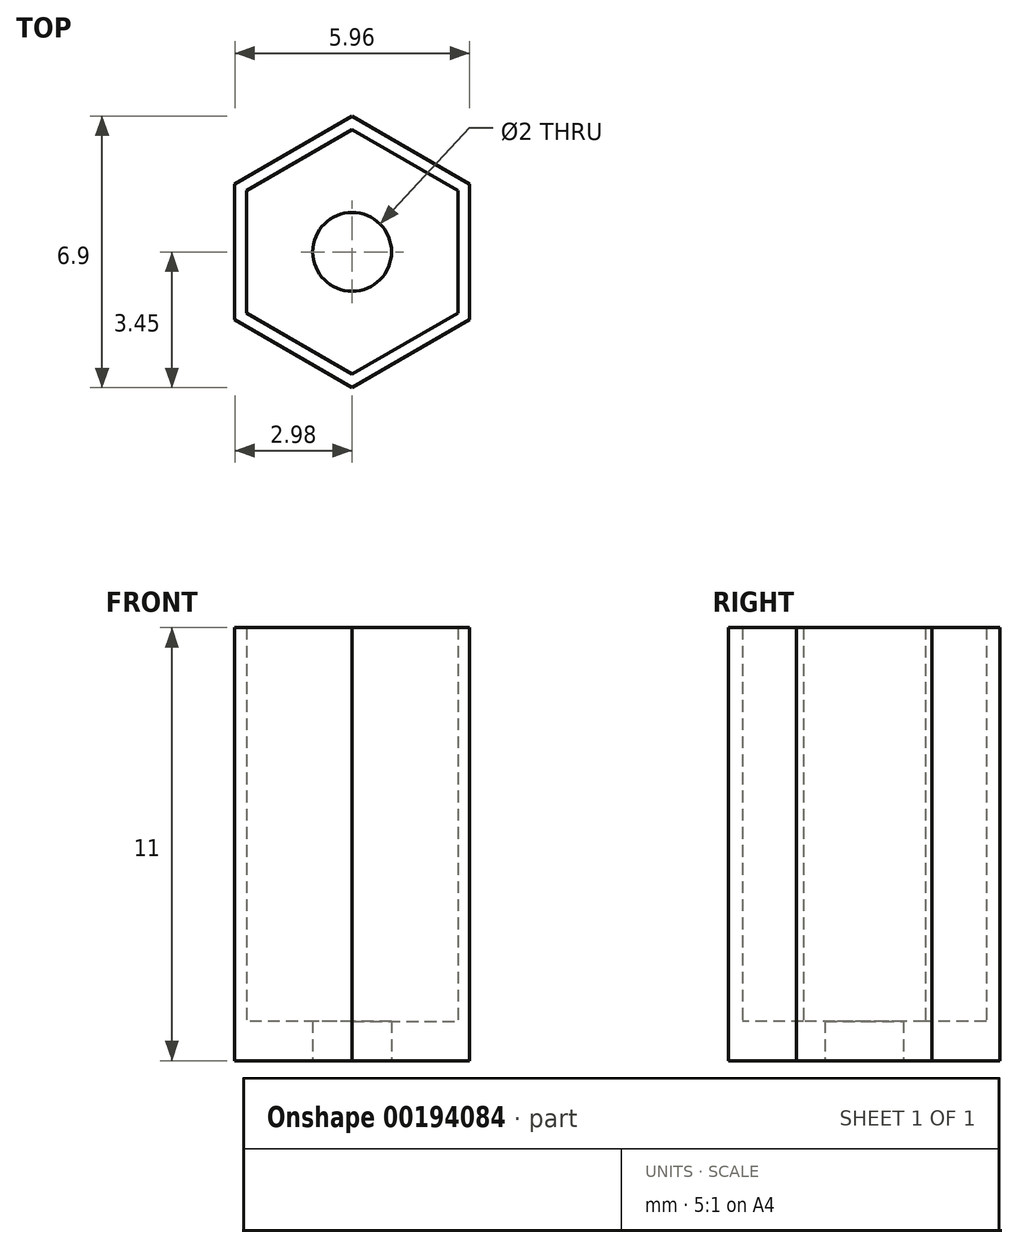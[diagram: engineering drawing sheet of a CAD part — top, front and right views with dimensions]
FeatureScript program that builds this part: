
annotation { "Feature Type Name" : "Feature", "Feature Type Description" : "" }
export const myFeature = defineFeature(function(context is Context, id is Id, definition is map)
    precondition{}
    {
        {
            var Q0;
            Q0=qCreatedBy(makeId("Top.planeOp"),FACE);
            var sketch = newSketch(context, id + "F0", { "sketchPlane" : qUnion([Q0])});
            skCircle(sketch, "E0.cCircle", {"center": v(0, 0) * mm, "radius": 2.68 * mm, "construction": true});
            skLineSegment(sketch, "E0.0", {"start": v(2.68, 1.55) * mm, "end": v(2.68, -1.55) * mm});
            skLineSegment(sketch, "E0.1", {"start": v(2.68, -1.55) * mm, "end": v(0, -3.1) * mm});
            skLineSegment(sketch, "E0.2", {"start": v(0, -3.1) * mm, "end": v(-2.68, -1.55) * mm});
            skLineSegment(sketch, "E0.3", {"start": v(-2.68, -1.55) * mm, "end": v(-2.68, 1.55) * mm});
            skLineSegment(sketch, "E0.4", {"start": v(-2.68, 1.55) * mm, "end": v(0, 3.1) * mm});
            skLineSegment(sketch, "E0.5", {"start": v(0, 3.1) * mm, "end": v(2.68, 1.55) * mm});
            skPoint(sketch, "E0.0.midPoint", {"position": v(2.68, 0) * mm});
            skLineSegment(sketch, "E1.0", {"start": v(-2.98, -1.72) * mm, "end": v(-2.98, 1.72) * mm});
            skLineSegment(sketch, "E1.1", {"start": v(0, 3.45) * mm, "end": v(2.98, 1.72) * mm});
            skLineSegment(sketch, "E1.2", {"start": v(2.98, 1.72) * mm, "end": v(2.98, -1.72) * mm});
            skLineSegment(sketch, "E1.3", {"start": v(-2.98, 1.72) * mm, "end": v(0, 3.45) * mm});
            skLineSegment(sketch, "E1.4", {"start": v(2.98, -1.72) * mm, "end": v(0, -3.45) * mm});
            skLineSegment(sketch, "E1.5", {"start": v(0, -3.45) * mm, "end": v(-2.98, -1.72) * mm});
            skCircle(sketch, "E2", {"center": v(0, 0) * mm, "radius": 1 * mm});
            skSolve(sketch);
        }
        {
            var Q0;
            Q0=makeQuery(id+"F0.imprint","IMPRINT",FACE,{"disambiguationData":[TD([[makeQuery(id+"F0.imprint","IMPRINT",EDGE,{"derivedFrom":sQuery(id+"F0.wireOp",EDGE,"E0.0")}),1.0]])]});
            extrude(context, id + "F1", {"entities" : qUnion([Q0]), "depth" : 11 * mm});
        }
        {
            var Q0;
            Q0=makeQuery(id+"F0.imprint","IMPRINT",FACE,{"disambiguationData":[TD([[makeQuery(id+"F0.imprint","IMPRINT",EDGE,{"derivedFrom":sQuery(id+"F0.wireOp",EDGE,"E0.0")}),-1.0]])]});
            extrude(context, id + "F2", {"entities" : qUnion([Q0]), "operationType" : NewBodyOperationType.ADD, "depth" : 1 * mm});
        }
    });
